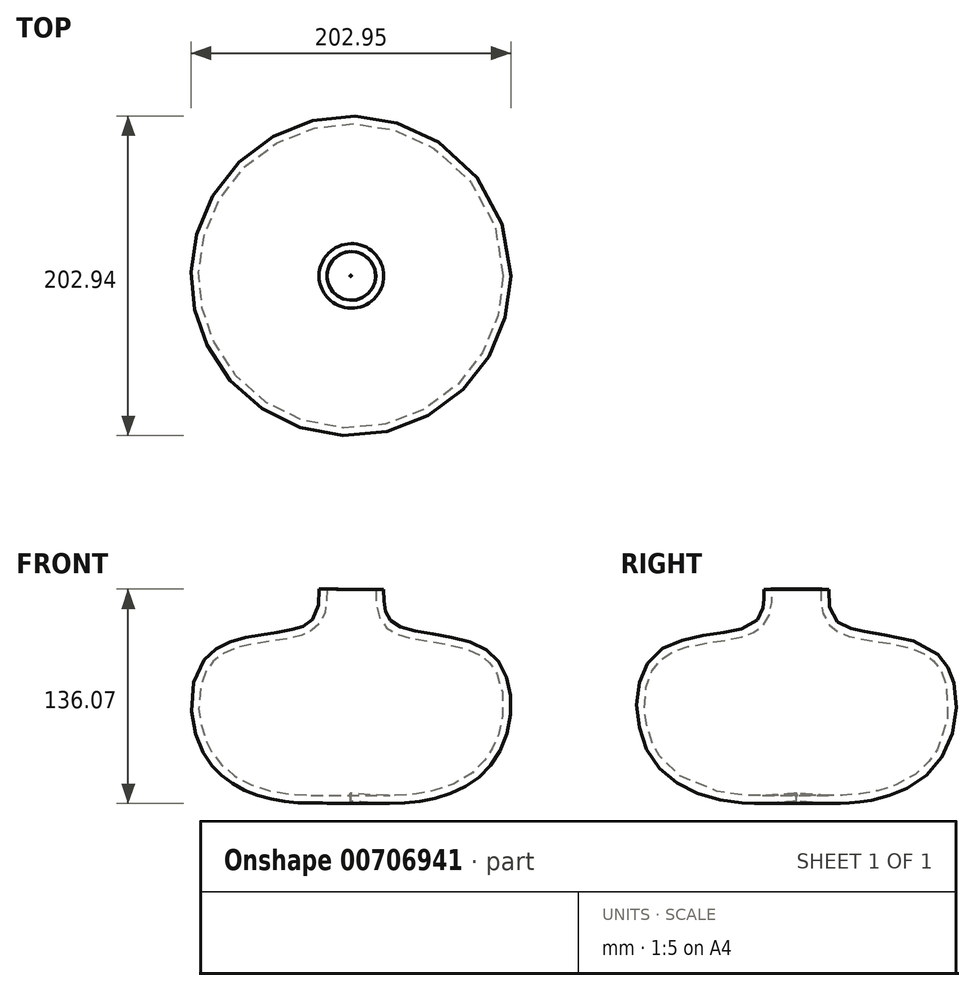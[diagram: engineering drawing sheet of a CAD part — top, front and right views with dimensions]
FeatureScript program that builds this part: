
annotation { "Feature Type Name" : "Feature", "Feature Type Description" : "" }
export const myFeature = defineFeature(function(context is Context, id is Id, definition is map)
    precondition{}
    {
        {
            var Q0;
            Q0=qCreatedBy(makeId("Front.planeOp"),FACE);
            var sketch = newSketch(context, id + "F0", { "sketchPlane" : qUnion([Q0])});
            skFitSpline(sketch, "E0", {"points": [v(20.94, 65.63) * mm, v(28.25, 43.43) * mm, v(88.96, 25.16) * mm, v(94.3, -38.09) * mm, v(48.77, -68.16) * mm, v(0, -69) * mm], "startDerivative": vector(-1.13, -190.51) * mm, "endDerivative": vector(-242.34, 18.66) * mm});
            skFitSpline(sketch, "E1.0", {"points": [v(15.94, 65.66) * mm, v(15.93, 63.68) * mm, v(15.9, 60.6) * mm, v(16.17, 56.38) * mm, v(16.6, 53.18) * mm, v(17.37, 49.97) * mm, v(18.62, 46.8) * mm, v(20.15, 44.26) * mm, v(21.7, 42.38) * mm, v(23.04, 41.07) * mm, v(24.54, 39.87) * mm, v(26.2, 38.79) * mm, v(27.94, 37.86) * mm, v(30.37, 36.8) * mm, v(33.6, 35.7) * mm, v(37.73, 34.66) * mm, v(42.1, 33.8) * mm, v(46.65, 33.04) * mm, v(51.33, 32.32) * mm, v(57.66, 31.34) * mm, v(63.98, 30.22) * mm, v(70, 28.78) * mm, v(74.27, 27.49) * mm, v(78.23, 25.96) * mm, v(81.8, 24.17) * mm, v(84.42, 22.44) * mm, v(86.26, 20.91) * mm, v(87.55, 19.66) * mm, v(88.75, 18.31) * mm, v(90.25, 16.39) * mm, v(91.9, 13.74) * mm, v(93.56, 10.2) * mm, v(95.3, 5.08) * mm, v(96.6, -1.97) * mm, v(96.77, -11) * mm, v(95.8, -18.57) * mm, v(94.4, -24.44) * mm, v(93.07, -28.67) * mm, v(91.72, -32.02) * mm, v(90.52, -34.55) * mm, v(89.24, -36.98) * mm, v(87.48, -39.83) * mm, v(85.13, -42.99) * mm, v(82.57, -45.89) * mm, v(78.89, -49.43) * mm, v(73.82, -53.29) * mm, v(67.12, -57.06) * mm, v(59.98, -60.05) * mm, v(53.8, -61.91) * mm, v(48.83, -63.07) * mm, v(43.86, -64.01) * mm, v(37.68, -64.81) * mm, v(30.27, -65.27) * mm, v(22.86, -65.33) * mm, v(12.94, -64.98) * mm, v(5.43, -64.4) * mm, v(0.38, -64.02) * mm]});
            skLineSegment(sketch, "E2", {"start": v(15.94, 65.66) * mm, "end": v(20.94, 65.63) * mm});
            skLineSegment(sketch, "E3", {"start": v(0.38, -64.02) * mm, "end": v(0, -69) * mm});
            skLineSegment(sketch, "E4", {"start": v(0.38, 52.7) * mm, "end": v(0, -54.39) * mm});
            skSolve(sketch);
        }
        {
            var Q0;
            Q0=makeQuery(id+"F0.imprint","IMPRINT",FACE,{"disambiguationData":[TD([[makeQuery(id+"F0.imprint","IMPRINT",EDGE,{"derivedFrom":sQuery(id+"F0.wireOp",EDGE,"E0")}),-1.0]])]});
            var Q1;
            Q1=sQuery(id+"F0.wireOp",EDGE,"E4");
            revolve(context, id + "F1", {"surfaceOperationType" : NewSurfaceOperationType.NEW, "entities" : qUnion([Q0]), "axis" : qUnion([Q1]), "revolveType" : RevolveType.FULL});
        }
    });
